# Revit family: Specialty-Equipment_TheSplashLab_Bath-Grab-Bars_TSL-GR45-18
name_source: partatom
category: Specialty Equipment
revit_build: Autodesk Revit 2016 (Build: 20160314_0715(x64)
units: mm (PartAtom-declared; Revit-internal decimal feet)

## family parameters
Cut with Voids When Loaded = No
Host = Face
OmniClass Number = 23.40.20.21.47
OmniClass Title = Bath Grab Bars
Part Type = Normal
Room Calculation Point = No
Round Connector Dimension = Use Diameter
Shared = No

## types (5) — shared parameters
Assembly Code = E1090
AssetType = Fixed
BIMObjectName = Specialty-Equipment_TheSplashLab_Bath-Grab-Bars_TSL-GR45-18
Category = SL_40_20_06
Default Elevation = 48"
DurationUnit = Year
Manufacturer = TheSplashLab
ManufacturerName = TheSplashLab
ManufacturerURL = https://thesplashlab.com
Model = TSL-GR45-18
NBSReference = SL_40_20_06
Name = Specialty-Equipment_TheSplashLab_Bath-Grab-Bars_TSL-GR45-18
NominalHeight = 4"
NominalLength = 21 1/2"
NominalWidth = 3 1/2"
Revision = 0
Uniclass2015Code = SL_40_20_06
Uniclass2015Title = Bars
Uniclass2015Version = UK_NBS_Uniclass2015_04_18
Version = 1
WarrantyDurationUnit = Year

## per-type parameters (varying)
| type | HousingMaterial |
| TSL-GR45-18CS | Brushed Stainless Steel |
| TSL-GR45-18CP | Brushed Copper |
| TSL-GR45-18BK | Brushed Black |
| TSL-GR45-18BR | Brushed Brass |
| TSL-GR45-18BZ | Brushed Bronze |

## geometry (parser evidence)
native form markers: Sweep x3
no freeform markers — native parametric forms only
